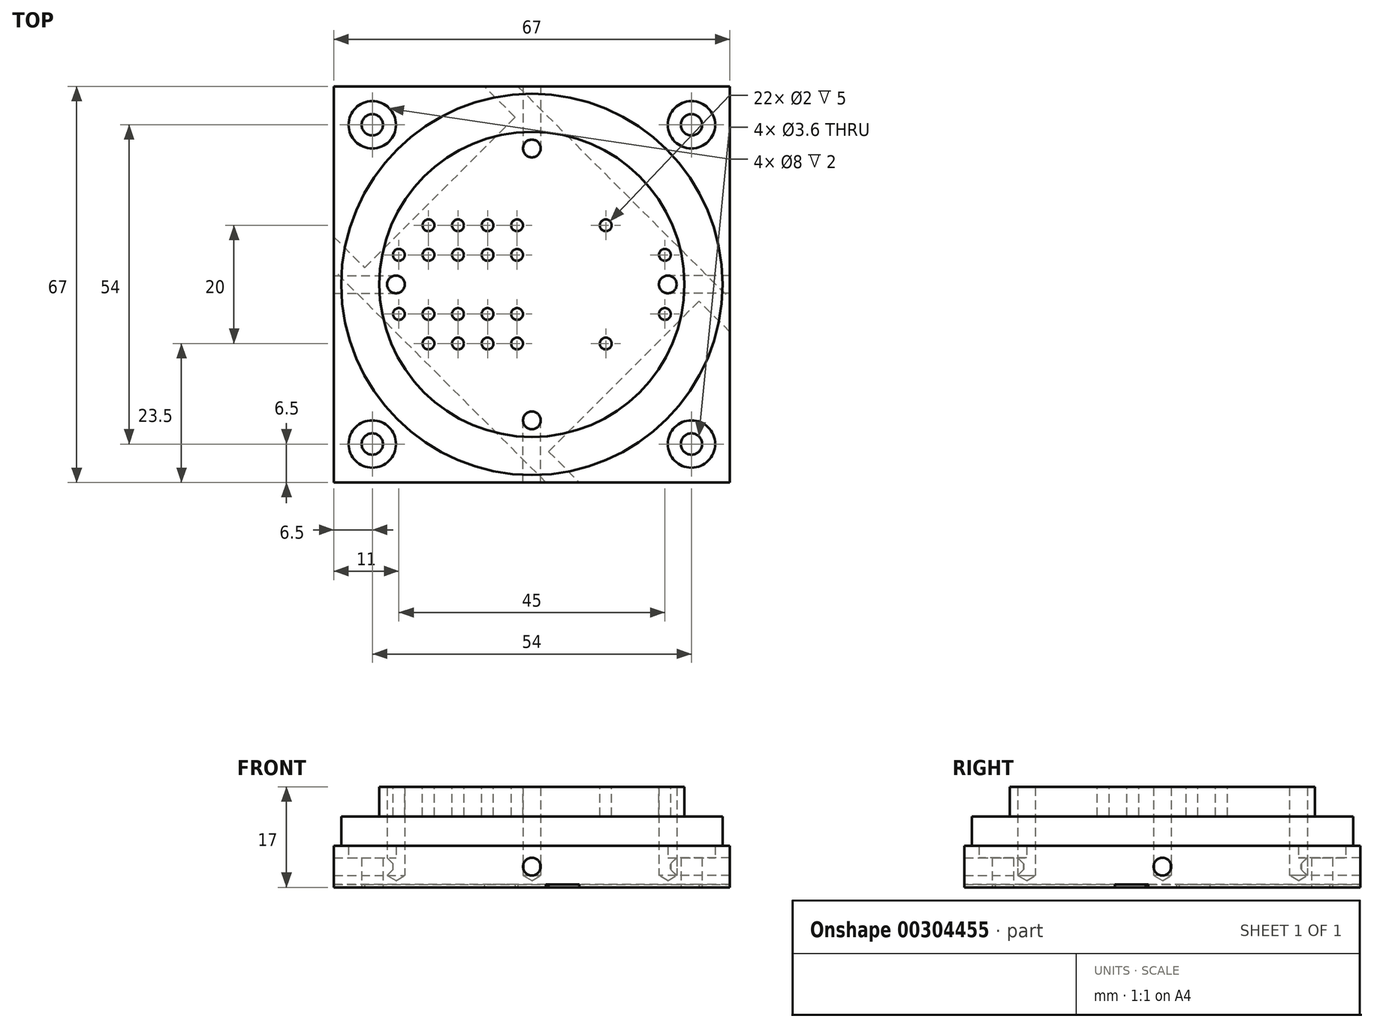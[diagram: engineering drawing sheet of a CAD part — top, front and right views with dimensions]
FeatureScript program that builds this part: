
annotation { "Feature Type Name" : "Feature", "Feature Type Description" : "" }
export const myFeature = defineFeature(function(context is Context, id is Id, definition is map)
    precondition{}
    {
        {
            var Q0;
            Q0=qCreatedBy(makeId("Top.planeOp"),FACE);
            var sketch = newSketch(context, id + "F0", { "sketchPlane" : qUnion([Q0])});
            skLineSegment(sketch, "E0.bottom", {"start": v(33.5, -33.5) * mm, "end": v(-33.5, -33.5) * mm});
            skLineSegment(sketch, "E0.top", {"start": v(33.5, 33.5) * mm, "end": v(-33.5, 33.5) * mm});
            skLineSegment(sketch, "E0.left", {"start": v(33.5, -33.5) * mm, "end": v(33.5, 33.5) * mm});
            skLineSegment(sketch, "E0.right", {"start": v(-33.5, -33.5) * mm, "end": v(-33.5, 33.5) * mm});
            skPoint(sketch, "E0.middle", {"position": v(0, 0) * mm});
            skCircle(sketch, "E1", {"center": v(0, 0) * mm, "radius": 75.5 * mm, "construction": true});
            skCircle(sketch, "E2", {"center": v(0, 0) * mm, "radius": 80 * mm, "construction": true});
            skSolve(sketch);
        }
        {
            var Q0;
            Q0 = qSketchRegion(id + "F0", true);
            extrude(context, id + "F1", {"entities" : qUnion([Q0]), "depth" : 7 * mm});
        }
        {
            var Q0;
            Q0=makeQuery(id+"F1.opExtrude","CAP_FACE",FACE,{"disambiguationData":[OSD([sQuery(id+"F0.wireOp",EDGE,"E0.bottom"),sQuery(id+"F0.wireOp",EDGE,"E0.top"),sQuery(id+"F0.wireOp",EDGE,"E0.left"),sQuery(id+"F0.wireOp",EDGE,"E0.right")])],"isStart":false});
            var sketch = newSketch(context, id + "F2", { "sketchPlane" : qUnion([Q0])});
            skCircle(sketch, "E3", {"center": v(0, 0) * mm, "radius": 32.25 * mm});
            skSolve(sketch);
        }
        {
            var Q0;
            Q0 = qSketchRegion(id + "F2", true);
            extrude(context, id + "F3", {"entities" : qUnion([Q0]), "operationType" : NewBodyOperationType.ADD, "depth" : 5 * mm});
        }
        {
            var Q0;
            Q0=makeQuery(id+"F3.opExtrude","CAP_FACE",FACE,{"disambiguationData":[OSD([sQuery(id+"F2.wireOp",EDGE,"E3")])],"isStart":false});
            var sketch = newSketch(context, id + "F4", { "sketchPlane" : qUnion([Q0])});
            skCircle(sketch, "E4", {"center": v(0, 0) * mm, "radius": 25.8 * mm});
            skSolve(sketch);
        }
        {
            var Q0;
            Q0 = qSketchRegion(id + "F4", true);
            extrude(context, id + "F5", {"entities" : qUnion([Q0]), "operationType" : NewBodyOperationType.ADD, "depth" : 5 * mm});
        }
        {
            var Q0;
            Q0=makeQuery(id+"F1.opExtrude","CAP_FACE",FACE,{"disambiguationData":[OSD([sQuery(id+"F0.wireOp",EDGE,"E0.bottom"),sQuery(id+"F0.wireOp",EDGE,"E0.top"),sQuery(id+"F0.wireOp",EDGE,"E0.left"),sQuery(id+"F0.wireOp",EDGE,"E0.right")])],"isStart":false});
            var sketch = newSketch(context, id + "F6", { "sketchPlane" : qUnion([Q0])});
            skPoint(sketch, "E5", {"position": v(-27, 27) * mm});
            skPoint(sketch, "E6", {"position": v(27, 27) * mm});
            skPoint(sketch, "E7", {"position": v(27, -27) * mm});
            skPoint(sketch, "E8", {"position": v(-27, -27) * mm});
            skLineSegment(sketch, "E9", {"start": v(27, 27) * mm, "end": v(-27, -27) * mm, "construction": true});
            skCircle(sketch, "E10", {"center": v(0, 0) * mm, "radius": 33.5 * mm, "construction": true});
            skCircle(sketch, "E11.cCircle", {"center": v(0, 0) * mm, "radius": 22 * mm, "construction": true});
            skLineSegment(sketch, "E11.0", {"start": v(31.11, 0) * mm, "end": v(0, -31.11) * mm, "construction": true});
            skLineSegment(sketch, "E11.1", {"start": v(0, -31.11) * mm, "end": v(-31.11, 0) * mm, "construction": true});
            skLineSegment(sketch, "E11.2", {"start": v(-31.11, 0) * mm, "end": v(0, 31.11) * mm, "construction": true});
            skLineSegment(sketch, "E11.3", {"start": v(0, 31.11) * mm, "end": v(31.11, 0) * mm, "construction": true});
            skPoint(sketch, "E11.0.midPoint", {"position": v(15.56, -15.56) * mm});
            skSolve(sketch);
        }
        {
            var Q0;
            Q0=sQuery(id+"F6.wireOp",VERTEX,"E5");
            var Q1;
            Q1=sQuery(id+"F6.wireOp",VERTEX,"E6");
            var Q2;
            Q2=sQuery(id+"F6.wireOp",VERTEX,"E7");
            var Q3;
            Q3=sQuery(id+"F6.wireOp",VERTEX,"E8");
            var Q4;
            Q4=makeQuery(id+"F1.opExtrude","SWEPT_BODY",BODY,{"disambiguationData":[OSD([sQuery(id+"F0.wireOp",EDGE,"E0.bottom"),sQuery(id+"F0.wireOp",EDGE,"E0.top"),sQuery(id+"F0.wireOp",EDGE,"E0.left"),sQuery(id+"F0.wireOp",EDGE,"E0.right")])]});
            hole(context, id + "F7", {"style" : HoleStyle.C_BORE, "endStyle" : HoleEndStyle.THROUGH, "holeDiameter" : 3.6 * mm, "cBoreDiameter" : 8 * mm, "cBoreDepth" : 2 * mm, "tappedDepth" : 12 * mm, "tapClearance" : 3, "locations" : qUnion([Q0, Q1, Q2, Q3]), "scope" : qUnion([Q4]), "startStyle" : HoleStartStyle.PART});
        }
        {
            var Q0;
            Q0=makeQuery(id+"F1.opExtrude","CAP_FACE",FACE,{"disambiguationData":[OSD([sQuery(id+"F0.wireOp",EDGE,"E0.bottom"),sQuery(id+"F0.wireOp",EDGE,"E0.top"),sQuery(id+"F0.wireOp",EDGE,"E0.left"),sQuery(id+"F0.wireOp",EDGE,"E0.right")])],"isStart":true});
            var sketch = newSketch(context, id + "F8", { "sketchPlane" : qUnion([Q0])});
            skLineSegment(sketch, "E12", {"start": v(38.52, 38.52) * mm, "end": v(-36.7, -36.7) * mm, "construction": true});
            skLineSegment(sketch, "E13", {"start": v(-39.23, 39.23) * mm, "end": v(37.27, -37.27) * mm, "construction": true});
            skPoint(sketch, "E14.endSnap0", {"position": v(33.5, 0) * mm});
            skLineSegment(sketch, "E15", {"start": v(9.95, 41.06) * mm, "end": v(-49.3, -18.2) * mm, "construction": true});
            skLineSegment(sketch, "E16", {"start": v(43.02, 11.9) * mm, "end": v(-17.29, -48.4) * mm, "construction": true});
            skLineSegment(sketch, "E17", {"start": v(-47.3, 16.18) * mm, "end": v(21.75, -52.87) * mm, "construction": true});
            skLineSegment(sketch, "E18", {"start": v(-15.83, 46.94) * mm, "end": v(57.48, -26.37) * mm, "construction": true});
            skLineSegment(sketch, "E19", {"start": v(12.65, 38.1) * mm, "end": v(-40.25, -14.8) * mm, "construction": true});
            skLineSegment(sketch, "E20", {"start": v(39.84, 14.38) * mm, "end": v(-15.51, -40.97) * mm, "construction": true});
            skLineSegment(sketch, "E21", {"start": v(2.39, 33.5) * mm, "end": v(-33.5, -2.39) * mm});
            skLineSegment(sketch, "E22", {"start": v(-33.5, -2.39) * mm, "end": v(-33.5, -8.04) * mm});
            skLineSegment(sketch, "E23", {"start": v(-33.5, -8.04) * mm, "end": v(-28.28, -2.83) * mm});
            skLineSegment(sketch, "E24", {"start": v(-28.28, -2.83) * mm, "end": v(-2.83, -28.28) * mm});
            skLineSegment(sketch, "E25", {"start": v(-2.83, -28.28) * mm, "end": v(-8.04, -33.5) * mm});
            skLineSegment(sketch, "E26", {"start": v(-8.04, -33.5) * mm, "end": v(-2.39, -33.5) * mm});
            skLineSegment(sketch, "E27", {"start": v(-2.39, -33.5) * mm, "end": v(33.5, 2.39) * mm});
            skLineSegment(sketch, "E28", {"start": v(33.5, 2.39) * mm, "end": v(33.5, 8.04) * mm});
            skLineSegment(sketch, "E29", {"start": v(33.5, 8.04) * mm, "end": v(28.28, 2.83) * mm});
            skLineSegment(sketch, "E30", {"start": v(28.28, 2.83) * mm, "end": v(2.83, 28.28) * mm});
            skLineSegment(sketch, "E31", {"start": v(2.83, 28.28) * mm, "end": v(8.04, 33.5) * mm});
            skLineSegment(sketch, "E32", {"start": v(8.04, 33.5) * mm, "end": v(2.39, 33.5) * mm});
            skSolve(sketch);
        }
        {
            var Q0;
            Q0 = qSketchRegion(id + "F8", true);
            extrude(context, id + "F9", {"entities" : qUnion([Q0]), "operationType" : NewBodyOperationType.REMOVE, "oppositeDirection" : true, "depth" : 0.5 * mm});
        }
        {
            var Q0;
            Q0=makeQuery(id+"F5.opExtrude","CAP_FACE",FACE,{"disambiguationData":[OSD([sQuery(id+"F4.wireOp",EDGE,"E4")])],"isStart":false});
            var sketch = newSketch(context, id + "F10", { "sketchPlane" : qUnion([Q0])});
            skCircle(sketch, "E33.0.1.0", {"center": v(-22.5, 5) * mm, "radius": 1 * mm});
            skCircle(sketch, "E33.1.1.0", {"center": v(-17.5, 5) * mm, "radius": 1 * mm});
            skCircle(sketch, "E33.1.2.0", {"center": v(-17.5, 10) * mm, "radius": 1 * mm});
            skCircle(sketch, "E33.2.1.0", {"center": v(-12.5, 5) * mm, "radius": 1 * mm});
            skCircle(sketch, "E33.2.2.0", {"center": v(-12.5, 10) * mm, "radius": 1 * mm});
            skCircle(sketch, "E33.7.2.0", {"center": v(12.5, 10) * mm, "radius": 1 * mm});
            skCircle(sketch, "E33.9.1.0", {"center": v(22.5, 5) * mm, "radius": 1 * mm});
            skCircle(sketch, "E34.0.1.0", {"center": v(-22.5, -5) * mm, "radius": 1 * mm});
            skCircle(sketch, "E34.1.1.0", {"center": v(-17.5, -5) * mm, "radius": 1 * mm});
            skCircle(sketch, "E34.1.2.0", {"center": v(-17.5, -10) * mm, "radius": 1 * mm});
            skCircle(sketch, "E34.2.1.0", {"center": v(-12.5, -5) * mm, "radius": 1 * mm});
            skCircle(sketch, "E34.2.2.0", {"center": v(-12.5, -10) * mm, "radius": 1 * mm});
            skCircle(sketch, "E34.7.2.0", {"center": v(12.5, -10) * mm, "radius": 1 * mm});
            skCircle(sketch, "E34.9.1.0", {"center": v(22.5, -5) * mm, "radius": 1 * mm});
            skLineSegment(sketch, "E35.bottom", {"start": v(7, 13) * mm, "end": v(18, 13) * mm, "construction": true});
            skLineSegment(sketch, "E35.top", {"start": v(7, -13) * mm, "end": v(18, -13) * mm, "construction": true});
            skLineSegment(sketch, "E35.left", {"start": v(7, 13) * mm, "end": v(7, -13) * mm, "construction": true});
            skLineSegment(sketch, "E35.right", {"start": v(18, 13) * mm, "end": v(18, -13) * mm, "construction": true});
            skLineSegment(sketch, "E36", {"start": v(-22.5, 5) * mm, "end": v(22.5, 5) * mm, "construction": true});
            skCircle(sketch, "E37.1.0.0", {"center": v(-7.5, 10) * mm, "radius": 1 * mm});
            skCircle(sketch, "E38.1.0.0", {"center": v(-7.5, -5) * mm, "radius": 1 * mm});
            skCircle(sketch, "E39.0.1.0", {"center": v(-7.5, 5) * mm, "radius": 1 * mm});
            skCircle(sketch, "E40.1.0.0", {"center": v(-7.5, -10) * mm, "radius": 1 * mm});
            skLineSegment(sketch, "E41", {"start": v(-22.5, -5) * mm, "end": v(22.5, -5) * mm, "construction": true});
            skLineSegment(sketch, "E42.bottom", {"start": v(-10.5, 13) * mm, "end": v(-4.5, 13) * mm, "construction": true});
            skLineSegment(sketch, "E42.top", {"start": v(-10.5, -13) * mm, "end": v(-4.5, -13) * mm, "construction": true});
            skLineSegment(sketch, "E42.left", {"start": v(-10.5, 13) * mm, "end": v(-10.5, -13) * mm, "construction": true});
            skLineSegment(sketch, "E42.right", {"start": v(-4.5, 13) * mm, "end": v(-4.5, -13) * mm, "construction": true});
            skLineSegment(sketch, "E43", {"start": v(-17.5, 10) * mm, "end": v(12.5, 10) * mm, "construction": true});
            skLineSegment(sketch, "E44", {"start": v(-17.5, -10) * mm, "end": v(12.5, -10) * mm, "construction": true});
            skLineSegment(sketch, "E45", {"start": v(-7.5, 10) * mm, "end": v(-7.5, -10) * mm, "construction": true});
            skLineSegment(sketch, "E46", {"start": v(-12.5, -10) * mm, "end": v(-12.5, 10) * mm, "construction": true});
            skLineSegment(sketch, "E47", {"start": v(-17.5, -10) * mm, "end": v(-17.5, 10) * mm, "construction": true});
            skLineSegment(sketch, "E48", {"start": v(12.5, 10) * mm, "end": v(12.5, -10) * mm, "construction": true});
            skCircle(sketch, "E49.1.0.0", {"center": v(-2.5, 10) * mm, "radius": 1 * mm});
            skCircle(sketch, "E49.1.0.1", {"center": v(-2.5, 5) * mm, "radius": 1 * mm});
            skCircle(sketch, "E49.1.0.2", {"center": v(-2.5, -5) * mm, "radius": 1 * mm});
            skCircle(sketch, "E49.1.0.3", {"center": v(-2.5, -10) * mm, "radius": 1 * mm});
            skLineSegment(sketch, "E49.direction1", {"start": v(-7.5, -10) * mm, "end": v(-2.5, -10) * mm, "construction": true});
            skSolve(sketch);
        }
        {
            var Q0;
            Q0 = qSketchRegion(id + "F10", true);
            extrude(context, id + "F11", {"entities" : qUnion([Q0]), "operationType" : NewBodyOperationType.REMOVE, "oppositeDirection" : true, "depth" : 5 * mm});
        }
        {
            var Q0;
            Q0=makeQuery(id+"F10.imprint","IMPRINT",FACE,{"disambiguationData":[TD([[makeQuery(id+"F10.imprint","IMPRINT",EDGE,{"derivedFrom":sQuery(id+"F10.wireOp",EDGE,"E33.0.1.0")}),-1.0]])]});
            var sketch = newSketch(context, id + "F12", { "sketchPlane" : qUnion([Q0])});
            skCircle(sketch, "E50", {"center": v(0, 0) * mm, "radius": 23 * mm, "construction": true});
            skLineSegment(sketch, "E51", {"start": v(0, -38.23) * mm, "end": v(0, 38.02) * mm, "construction": true});
            skLineSegment(sketch, "E52", {"start": v(37.92, 0) * mm, "end": v(-38.46, 0) * mm, "construction": true});
            skPoint(sketch, "E53", {"position": v(0, -23) * mm});
            skPoint(sketch, "E54", {"position": v(23, 0) * mm});
            skPoint(sketch, "E55", {"position": v(-23, 0) * mm});
            skPoint(sketch, "E56", {"position": v(0, 23) * mm});
            skSolve(sketch);
        }
        {
            var Q0;
            Q0=sQuery(id+"F12.wireOp",VERTEX,"E53");
            var Q1;
            Q1=sQuery(id+"F12.wireOp",VERTEX,"E54");
            var Q2;
            Q2=sQuery(id+"F12.wireOp",VERTEX,"E55");
            var Q3;
            Q3=sQuery(id+"F12.wireOp",VERTEX,"E56");
            var Q4;
            Q4=makeQuery(id+"F1.opExtrude","SWEPT_BODY",BODY,{"disambiguationData":[OSD([sQuery(id+"F0.wireOp",EDGE,"E0.bottom"),sQuery(id+"F0.wireOp",EDGE,"E0.top"),sQuery(id+"F0.wireOp",EDGE,"E0.left"),sQuery(id+"F0.wireOp",EDGE,"E0.right")])]});
            hole(context, id + "F13", {"style" : HoleStyle.SIMPLE, "endStyle" : HoleEndStyle.BLIND, "holeDiameter" : 3 * mm, "holeDepth" : 15 * mm, "isTappedThrough" : true, "tappedDepth" : 12 * mm, "tapClearance" : 3, "locations" : qUnion([Q0, Q1, Q2, Q3]), "scope" : qUnion([Q4]), "startStyle" : HoleStartStyle.PART});
        }
        {
            var Q0;
            Q0=makeQuery(id+"F1.opExtrude","SWEPT_FACE",FACE,{"disambiguationData":[OSD([sQuery(id+"F0.wireOp",EDGE,"E0.bottom")])]});
            var sketch = newSketch(context, id + "F14", { "sketchPlane" : qUnion([Q0])});
            skPoint(sketch, "E57", {"position": v(0, 3.5) * mm});
            skSolve(sketch);
        }
        {
            var Q0;
            Q0=sQuery(id+"F14.wireOp",VERTEX,"E57");
            var Q1;
            Q1=makeQuery(id+"F1.opExtrude","SWEPT_BODY",BODY,{"disambiguationData":[OSD([sQuery(id+"F0.wireOp",EDGE,"E0.bottom"),sQuery(id+"F0.wireOp",EDGE,"E0.top"),sQuery(id+"F0.wireOp",EDGE,"E0.left"),sQuery(id+"F0.wireOp",EDGE,"E0.right")])]});
            hole(context, id + "F15", {"style" : HoleStyle.SIMPLE, "endStyle" : HoleEndStyle.BLIND, "holeDiameter" : 3 * mm, "holeDepth" : 10 * mm, "isTappedThrough" : true, "tappedDepth" : 12 * mm, "tapClearance" : 3, "locations" : qUnion([Q0]), "scope" : qUnion([Q1]), "startStyle" : HoleStartStyle.PART});
        }
        {
            var Q0;
            Q0=makeQuery(id+"F1.opExtrude","SWEPT_FACE",FACE,{"disambiguationData":[OSD([sQuery(id+"F0.wireOp",EDGE,"E0.left")])]});
            var sketch = newSketch(context, id + "F16", { "sketchPlane" : qUnion([Q0])});
            skPoint(sketch, "E58", {"position": v(0, 3.5) * mm});
            skSolve(sketch);
        }
        {
            var Q0;
            Q0=sQuery(id+"F16.wireOp",VERTEX,"E58");
            var Q1;
            Q1=makeQuery(id+"F1.opExtrude","SWEPT_BODY",BODY,{"disambiguationData":[OSD([sQuery(id+"F0.wireOp",EDGE,"E0.bottom"),sQuery(id+"F0.wireOp",EDGE,"E0.top"),sQuery(id+"F0.wireOp",EDGE,"E0.left"),sQuery(id+"F0.wireOp",EDGE,"E0.right")])]});
            hole(context, id + "F17", {"style" : HoleStyle.SIMPLE, "endStyle" : HoleEndStyle.BLIND, "holeDiameter" : 3 * mm, "holeDepth" : 10 * mm, "isTappedThrough" : true, "tappedDepth" : 12 * mm, "tapClearance" : 3, "locations" : qUnion([Q0]), "scope" : qUnion([Q1]), "startStyle" : HoleStartStyle.PART});
        }
        {
            var Q0;
            Q0=makeQuery(id+"F1.opExtrude","SWEPT_FACE",FACE,{"disambiguationData":[OSD([sQuery(id+"F0.wireOp",EDGE,"E0.top")])]});
            var sketch = newSketch(context, id + "F18", { "sketchPlane" : qUnion([Q0])});
            skPoint(sketch, "E59", {"position": v(0, 3.5) * mm});
            skSolve(sketch);
        }
        {
            var Q0;
            Q0=sQuery(id+"F18.wireOp",VERTEX,"E59");
            var Q1;
            Q1=makeQuery(id+"F1.opExtrude","SWEPT_BODY",BODY,{"disambiguationData":[OSD([sQuery(id+"F0.wireOp",EDGE,"E0.bottom"),sQuery(id+"F0.wireOp",EDGE,"E0.top"),sQuery(id+"F0.wireOp",EDGE,"E0.left"),sQuery(id+"F0.wireOp",EDGE,"E0.right")])]});
            hole(context, id + "F19", {"style" : HoleStyle.SIMPLE, "endStyle" : HoleEndStyle.BLIND, "holeDiameter" : 3 * mm, "holeDepth" : 10 * mm, "isTappedThrough" : true, "tappedDepth" : 12 * mm, "tapClearance" : 3, "locations" : qUnion([Q0]), "scope" : qUnion([Q1]), "startStyle" : HoleStartStyle.PART});
        }
        {
            var Q0;
            Q0=makeQuery(id+"F1.opExtrude","SWEPT_FACE",FACE,{"disambiguationData":[OSD([sQuery(id+"F0.wireOp",EDGE,"E0.right")])]});
            var sketch = newSketch(context, id + "F20", { "sketchPlane" : qUnion([Q0])});
            skPoint(sketch, "E60", {"position": v(0, 3.5) * mm});
            skSolve(sketch);
        }
        {
            var Q0;
            Q0=sQuery(id+"F20.wireOp",VERTEX,"E60");
            var Q1;
            Q1=makeQuery(id+"F1.opExtrude","SWEPT_BODY",BODY,{"disambiguationData":[OSD([sQuery(id+"F0.wireOp",EDGE,"E0.bottom"),sQuery(id+"F0.wireOp",EDGE,"E0.top"),sQuery(id+"F0.wireOp",EDGE,"E0.left"),sQuery(id+"F0.wireOp",EDGE,"E0.right")])]});
            hole(context, id + "F21", {"style" : HoleStyle.SIMPLE, "endStyle" : HoleEndStyle.BLIND, "holeDiameter" : 3 * mm, "holeDepth" : 10 * mm, "isTappedThrough" : true, "tappedDepth" : 12 * mm, "tapClearance" : 3, "locations" : qUnion([Q0]), "scope" : qUnion([Q1]), "startStyle" : HoleStartStyle.PART});
        }
    });
